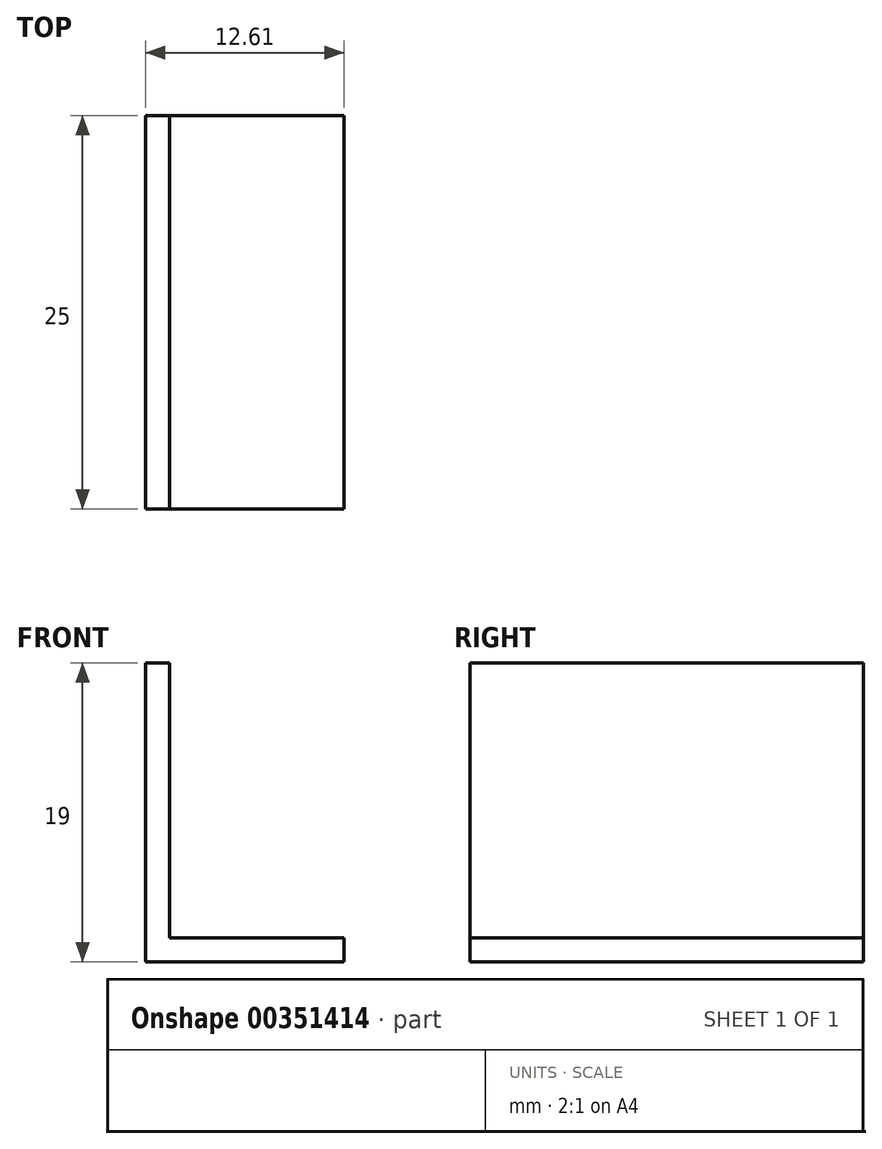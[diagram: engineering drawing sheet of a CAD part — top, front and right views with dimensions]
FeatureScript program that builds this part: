
annotation { "Feature Type Name" : "Feature", "Feature Type Description" : "" }
export const myFeature = defineFeature(function(context is Context, id is Id, definition is map)
    precondition{}
    {
        {
            var Q0;
            Q0=qCreatedBy(makeId("Front.planeOp"),FACE);
            var sketch = newSketch(context, id + "F0", { "sketchPlane" : qUnion([Q0])});
            skLineSegment(sketch, "E0.bottom", {"start": v(0, 0) * mm, "end": v(-1.52, 0) * mm});
            skLineSegment(sketch, "E0.top", {"start": v(0, 19) * mm, "end": v(-1.52, 19) * mm});
            skLineSegment(sketch, "E0.left", {"start": v(0, 0) * mm, "end": v(0, 19) * mm});
            skLineSegment(sketch, "E0.right", {"start": v(-1.52, 0) * mm, "end": v(-1.52, 19) * mm});
            skLineSegment(sketch, "E1.bottom", {"start": v(0, 0) * mm, "end": v(11.1, 0) * mm});
            skLineSegment(sketch, "E1.top", {"start": v(0, 1.52) * mm, "end": v(11.1, 1.52) * mm});
            skLineSegment(sketch, "E1.left", {"start": v(0, 0) * mm, "end": v(0, 1.52) * mm});
            skLineSegment(sketch, "E1.right", {"start": v(11.1, 0) * mm, "end": v(11.1, 1.52) * mm});
            skSolve(sketch);
        }
        {
            var Q0;
            Q0 = qSketchRegion(id + "F0", true);
            extrude(context, id + "F1", {"entities" : qUnion([Q0]), "depth" : 25 * mm});
        }
    });
